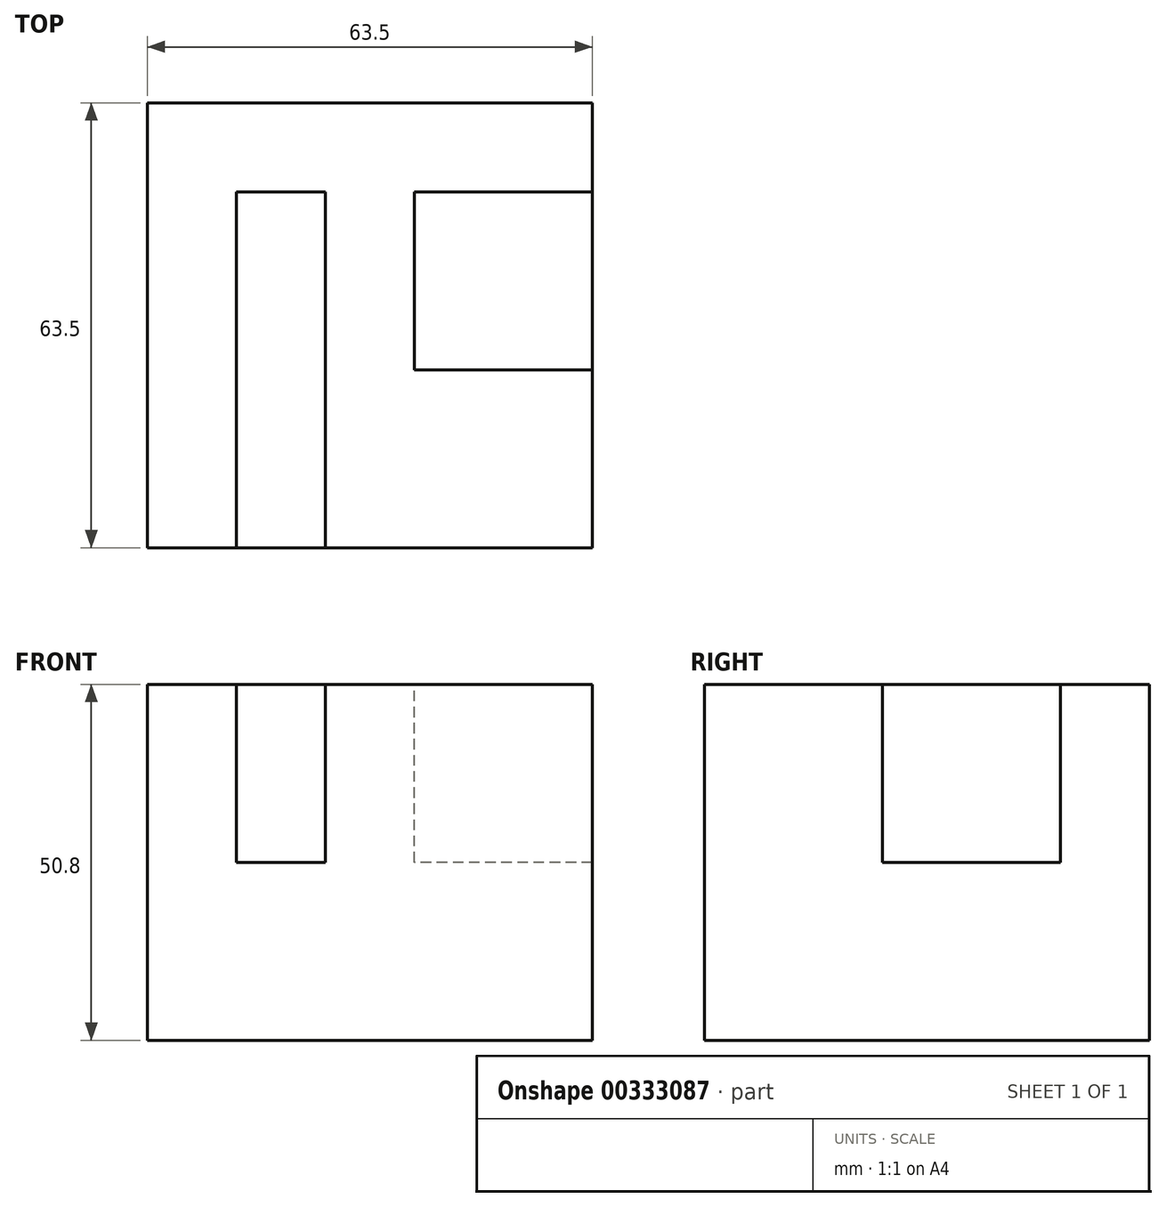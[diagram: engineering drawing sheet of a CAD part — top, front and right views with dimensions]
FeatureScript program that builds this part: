
annotation { "Feature Type Name" : "Feature", "Feature Type Description" : "" }
export const myFeature = defineFeature(function(context is Context, id is Id, definition is map)
    precondition{}
    {
        {
            var Q0;
            Q0=qCreatedBy(makeId("Front.planeOp"),FACE);
            var sketch = newSketch(context, id + "F0", { "sketchPlane" : qUnion([Q0])});
            skLineSegment(sketch, "E0", {"start": v(-35.63, 2.83) * mm, "end": v(-35.63, -47.97) * mm});
            skLineSegment(sketch, "E1", {"start": v(-35.63, -47.97) * mm, "end": v(27.87, -47.97) * mm});
            skLineSegment(sketch, "E2", {"start": v(27.87, -47.97) * mm, "end": v(27.87, 2.83) * mm});
            skLineSegment(sketch, "E3", {"start": v(-35.63, 2.83) * mm, "end": v(27.87, 2.83) * mm});
            skSolve(sketch);
        }
        {
            var Q0;
            Q0 = qSketchRegion(id + "F0", true);
            extrude(context, id + "F1", {"entities" : qUnion([Q0]), "depth" : 63.5 * mm});
        }
        {
            var Q0;
            Q0=makeQuery(id+"F1.opExtrude","SWEPT_FACE",FACE,{"disambiguationData":[OSD([sQuery(id+"F0.wireOp",EDGE,"E3")])]});
            var sketch = newSketch(context, id + "F2", { "sketchPlane" : qUnion([Q0])});
            skLineSegment(sketch, "E4", {"start": v(-22.93, -63.5) * mm, "end": v(-22.93, -12.7) * mm});
            skLineSegment(sketch, "E5", {"start": v(-22.93, -12.7) * mm, "end": v(-10.23, -12.7) * mm});
            skLineSegment(sketch, "E6", {"start": v(-10.23, -12.7) * mm, "end": v(-10.23, -63.5) * mm});
            skLineSegment(sketch, "E7", {"start": v(27.87, -12.7) * mm, "end": v(2.47, -12.7) * mm});
            skLineSegment(sketch, "E8", {"start": v(2.47, -12.7) * mm, "end": v(2.47, -38.1) * mm});
            skLineSegment(sketch, "E9", {"start": v(2.47, -38.1) * mm, "end": v(27.87, -38.1) * mm});
            skSolve(sketch);
        }
        {
            var Q0;
            Q0 = qSketchRegion(id + "F2", true);
            var Q1;
            {var subQ0=sQuery(id+"F2.wireOp",EDGE,"E4");Q1=makeQuery(id+"F2.imprint","IMPRINT",FACE,{"disambiguationData":[TD([[makeQuery(id+"F2.imprint","IMPRINT",EDGE,{"derivedFrom":subQ0}),-1.0]])]});}
            extrude(context, id + "F3", {"entities" : qUnion([Q0, Q1]), "operationType" : NewBodyOperationType.REMOVE, "oppositeDirection" : true, "depth" : 25.4 * mm});
        }
        {
            var Q0;
            {var subQ0=sQuery(id+"F2.wireOp",EDGE,"E7");Q0=makeQuery(id+"F2.imprint","IMPRINT",FACE,{"disambiguationData":[TD([[makeQuery(id+"F2.imprint","IMPRINT",EDGE,{"derivedFrom":subQ0}),1.0]])]});}
            extrude(context, id + "F4", {"entities" : qUnion([Q0]), "operationType" : NewBodyOperationType.REMOVE, "oppositeDirection" : true, "depth" : 25.4 * mm});
        }
    });
